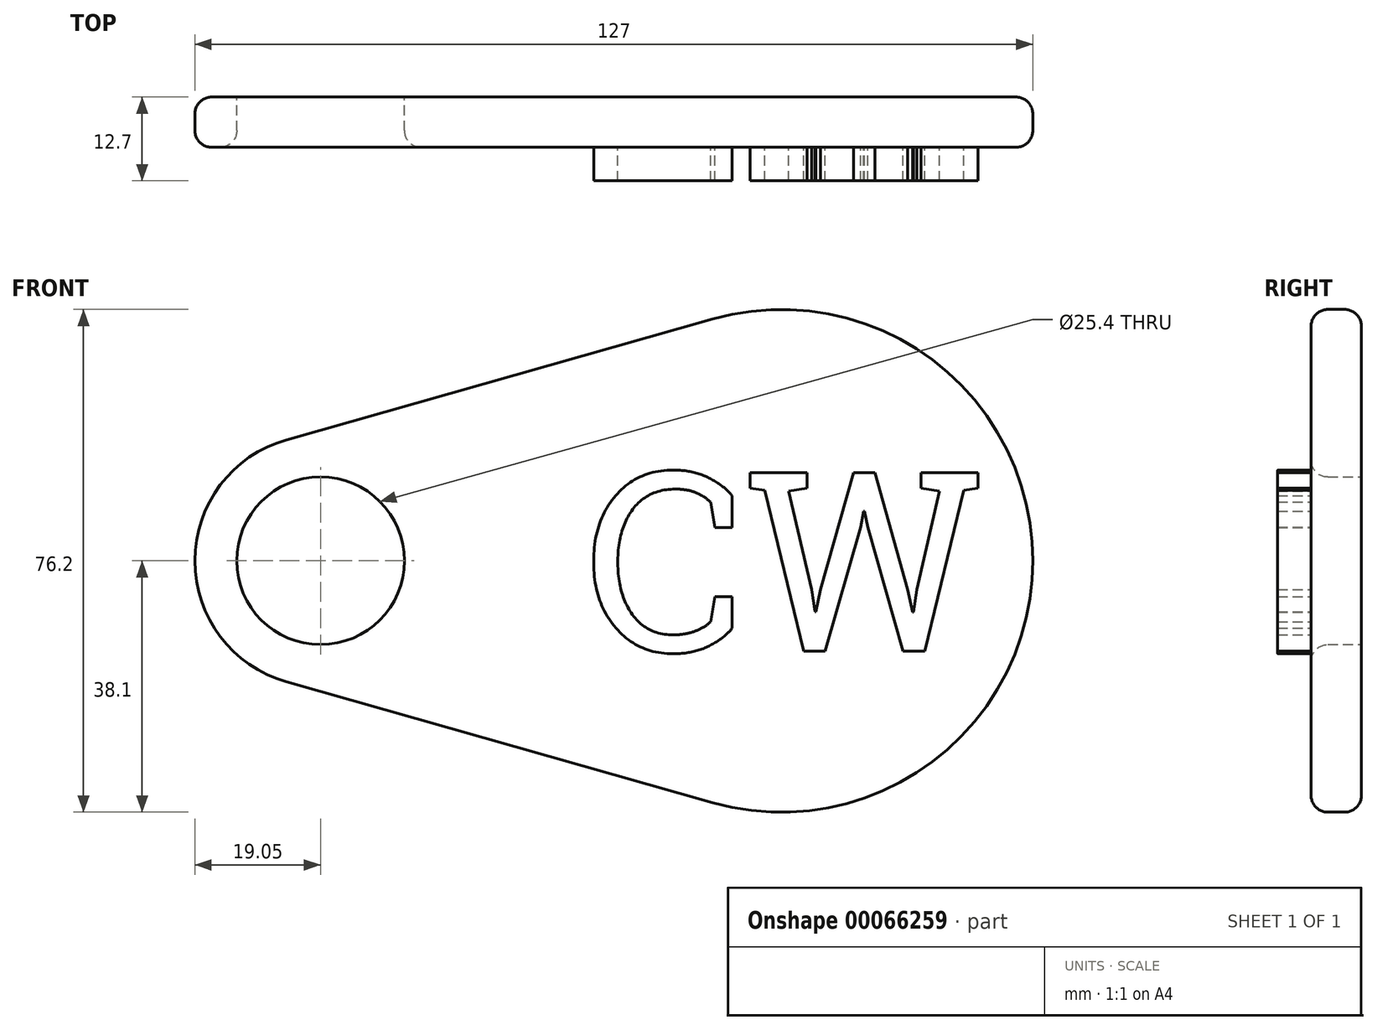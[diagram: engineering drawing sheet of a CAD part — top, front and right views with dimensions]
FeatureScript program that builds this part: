
annotation { "Feature Type Name" : "Feature", "Feature Type Description" : "" }
export const myFeature = defineFeature(function(context is Context, id is Id, definition is map)
    precondition{}
    {
        {
            var Q0;
            Q0=qCreatedBy(makeId("Front.planeOp"),FACE);
            var sketch = newSketch(context, id + "F0", { "sketchPlane" : qUnion([Q0])});
            skCircle(sketch, "E0", {"center": v(-69.85, 0) * mm, "radius": 19.05 * mm});
            skCircle(sketch, "E1", {"center": v(0, 0) * mm, "radius": 38.1 * mm});
            skLineSegment(sketch, "E2", {"start": v(-75.05, 18.33) * mm, "end": v(-10.4, 36.66) * mm});
            skLineSegment(sketch, "E3", {"start": v(-75.05, -18.33) * mm, "end": v(-10.4, -36.66) * mm});
            skSolve(sketch);
        }
        {
            var Q0;
            {var subQ0=sQuery(id+"F0.wireOp",EDGE,"E1");var subQ1=makeQuery(id+"F0.imprint","INTERSECT",VERTEX,{"derivedFrom":[subQ0,sQuery(id+"F0.wireOp",EDGE,"E2")]});Q0=makeQuery(id+"F0.imprint","IMPRINT",FACE,{"disambiguationData":[TD([[makeQuery(id+"F0.imprint","IMPRINT",EDGE,{"disambiguationData":[TD([[subQ1,-1.0]])],"derivedFrom":subQ0}),1.0]])]});}
            var Q1;
            {var subQ0=sQuery(id+"F0.wireOp",EDGE,"E2");Q1=makeQuery(id+"F0.imprint","IMPRINT",FACE,{"disambiguationData":[TD([[makeQuery(id+"F0.imprint","IMPRINT",EDGE,{"derivedFrom":subQ0}),-1.0]])]});}
            var Q2;
            {var subQ0=sQuery(id+"F0.wireOp",EDGE,"E0");var subQ1=makeQuery(id+"F0.imprint","INTERSECT",VERTEX,{"derivedFrom":[subQ0,sQuery(id+"F0.wireOp",EDGE,"E2")]});Q2=makeQuery(id+"F0.imprint","IMPRINT",FACE,{"disambiguationData":[TD([[makeQuery(id+"F0.imprint","IMPRINT",EDGE,{"disambiguationData":[TD([[subQ1,-1.0]])],"derivedFrom":subQ0}),1.0]])]});}
            extrude(context, id + "F1", {"entities" : qUnion([Q0, Q1, Q2]), "depth" : 7.62 * mm});
        }
        {
            var Q0;
            Q0=makeQuery(id+"F1.opExtrude","CAP_FACE",FACE,{"disambiguationData":[OSD([sQuery(id+"F0.wireOp",EDGE,"E0"),sQuery(id+"F0.wireOp",EDGE,"E1"),sQuery(id+"F0.wireOp",EDGE,"E2"),sQuery(id+"F0.wireOp",EDGE,"E3")])],"isStart":true});
            var sketch = newSketch(context, id + "F2", { "sketchPlane" : qUnion([Q0])});
            skCircle(sketch, "E4", {"center": v(69.85, 0) * mm, "radius": 12.7 * mm});
            skSolve(sketch);
        }
        {
            var Q0;
            Q0=makeQuery(id+"F2.imprint","IMPRINT",FACE,{"disambiguationData":[TD([[makeQuery(id+"F2.imprint","IMPRINT",EDGE,{"derivedFrom":sQuery(id+"F2.wireOp",EDGE,"E4")}),1.0]])]});
            extrude(context, id + "F3", {"entities" : qUnion([Q0]), "operationType" : NewBodyOperationType.REMOVE, "oppositeDirection" : true, "depth" : 25.4 * mm});
        }
        {
            var Q0;
            Q0=makeQuery(id+"F1.opExtrude","CAP_FACE",FACE,{"disambiguationData":[OSD([sQuery(id+"F0.wireOp",EDGE,"E0"),sQuery(id+"F0.wireOp",EDGE,"E1"),sQuery(id+"F0.wireOp",EDGE,"E2"),sQuery(id+"F0.wireOp",EDGE,"E3")])],"isStart":false});
            var sketch = newSketch(context, id + "F4", { "sketchPlane" : qUnion([Q0])});
            skPoint(sketch, "E5.rect.middle", {"position": v(0, 0) * mm});
            skText(sketch, "E6", { "text": "CW", "fontName": "RobotoSlab-Regular.ttf"});
            const initialGuessF4  = {"E6": [-0.02978, -0.0137, 1, 0, 0.02741]};
            skSetInitialGuess(sketch, initialGuessF4);
            skSolve(sketch);
        }
        {
            var Q0;
            Q0 = qSketchRegion(id + "F4", true);
            extrude(context, id + "F5", {"entities" : qUnion([Q0]), "operationType" : NewBodyOperationType.ADD, "depth" : 5.08 * mm});
        }
        {
            var Q0;
            Q0=makeQuery(id+"F1.opExtrude","CAP_EDGE",EDGE,{"disambiguationData":[OSD([sQuery(id+"F0.wireOp",EDGE,"E3")])],"isStart":false});
            var Q1;
            Q1=makeQuery(id+"F1.opExtrude","CAP_EDGE",EDGE,{"disambiguationData":[OSD([sQuery(id+"F0.wireOp",EDGE,"E0")])],"isStart":false});
            var Q2;
            Q2=makeQuery(id+"F1.opExtrude","CAP_EDGE",EDGE,{"disambiguationData":[OSD([sQuery(id+"F0.wireOp",EDGE,"E2")])],"isStart":false});
            var Q3;
            Q3=makeQuery(id+"F1.opExtrude","CAP_EDGE",EDGE,{"disambiguationData":[OSD([sQuery(id+"F0.wireOp",EDGE,"E1")])],"isStart":false});
            fillet(context, id + "F6", {"entities" : qUnion([Q0, Q1, Q2, Q3]), "radius" : 2.54 * mm, "tangentPropagation" : true, "allowEdgeOverflow" : false});
        }
        {
            var Q0;
            Q0=makeQuery(id+"F1.opExtrude","CAP_EDGE",EDGE,{"disambiguationData":[OSD([sQuery(id+"F0.wireOp",EDGE,"E2")])],"isStart":true});
            var Q1;
            Q1=makeQuery(id+"F1.opExtrude","CAP_EDGE",EDGE,{"disambiguationData":[OSD([sQuery(id+"F0.wireOp",EDGE,"E1")])],"isStart":true});
            var Q2;
            Q2=makeQuery(id+"F1.opExtrude","CAP_EDGE",EDGE,{"disambiguationData":[OSD([sQuery(id+"F0.wireOp",EDGE,"E3")])],"isStart":true});
            var Q3;
            Q3=makeQuery(id+"F1.opExtrude","CAP_EDGE",EDGE,{"disambiguationData":[OSD([sQuery(id+"F0.wireOp",EDGE,"E0")])],"isStart":true});
            var Q4;
            Q4=makeQuery(id+"F3.boolean.opBoolean","COPY",EDGE,{"derivedFrom":makeQuery(id+"F3.opExtrude","CAP_EDGE",EDGE,{"disambiguationData":[OSD([sQuery(id+"F2.wireOp",EDGE,"E4")])],"isStart":true})});
            var Q5;
            Q5=makeQuery(id+"F3.boolean.opBoolean","INTERSECT",EDGE,{"derivedFrom":[makeQuery(id+"F1.opExtrude","CAP_FACE",FACE,{"disambiguationData":[OSD([sQuery(id+"F0.wireOp",EDGE,"E0"),sQuery(id+"F0.wireOp",EDGE,"E1"),sQuery(id+"F0.wireOp",EDGE,"E2"),sQuery(id+"F0.wireOp",EDGE,"E3")])],"isStart":false}),makeQuery(id+"F3.opExtrude","SWEPT_FACE",FACE,{"disambiguationData":[OSD([sQuery(id+"F2.wireOp",EDGE,"E4")])]})]});
            fillet(context, id + "F7", {"entities" : qUnion([Q0, Q1, Q2, Q3, Q4, Q5]), "radius" : 2.54 * mm, "tangentPropagation" : true, "allowEdgeOverflow" : false});
        }
    });
